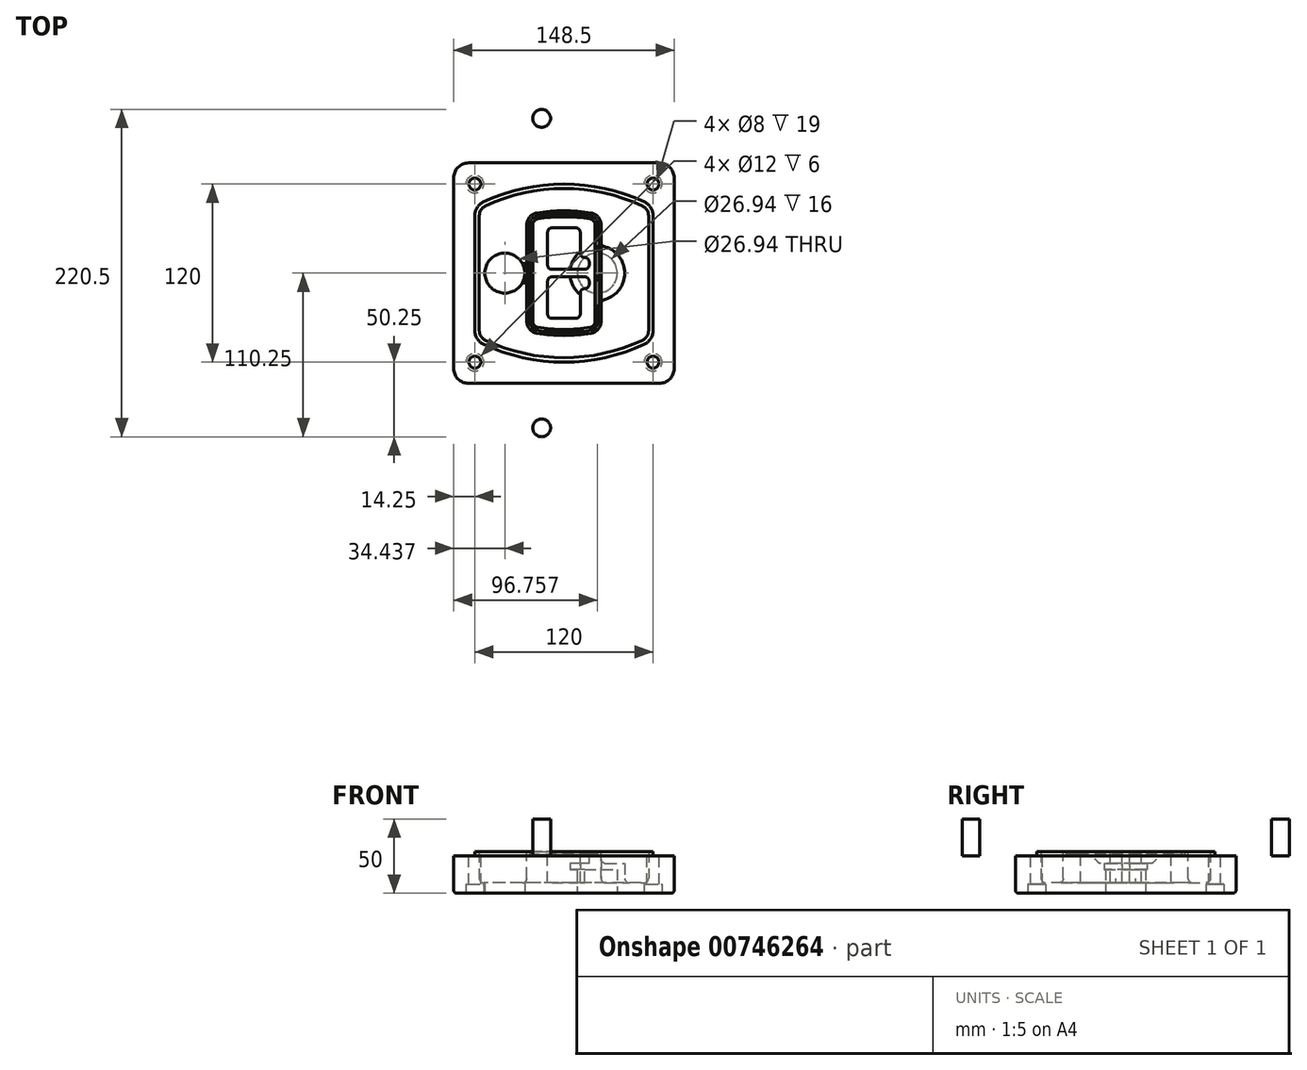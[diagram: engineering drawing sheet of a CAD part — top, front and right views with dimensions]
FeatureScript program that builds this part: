
annotation { "Feature Type Name" : "Feature", "Feature Type Description" : "" }
export const myFeature = defineFeature(function(context is Context, id is Id, definition is map)
    precondition{}
    {
        {
            var Q0;
            Q0=qCreatedBy(makeId("Top.planeOp"),FACE);
            var sketch = newSketch(context, id + "F0", { "sketchPlane" : qUnion([Q0])});
            skPoint(sketch, "E0.rect.middle", {"position": v(0, 0) * mm});
            skLineSegment(sketch, "E1.bottom", {"start": v(-64.25, -74.25) * mm, "end": v(64.25, -74.25) * mm});
            skLineSegment(sketch, "E1.top", {"start": v(-64.25, 74.25) * mm, "end": v(64.25, 74.25) * mm});
            skLineSegment(sketch, "E1.left", {"start": v(-74.25, -64.25) * mm, "end": v(-74.25, 64.25) * mm});
            skLineSegment(sketch, "E1.right", {"start": v(74.25, -64.25) * mm, "end": v(74.25, 64.25) * mm});
            skLineSegment(sketch, "E2", {"start": v(-74.25, 74.25) * mm, "end": v(74.25, -74.25) * mm, "construction": true});
            skLineSegment(sketch, "E3", {"start": v(74.25, 74.25) * mm, "end": v(-74.25, -74.25) * mm, "construction": true});
            skCircle(sketch, "E4", {"center": v(-60, 60) * mm, "radius": 4 * mm});
            skCircle(sketch, "E5", {"center": v(60, 60) * mm, "radius": 4 * mm});
            skCircle(sketch, "E6", {"center": v(60, -60) * mm, "radius": 4 * mm});
            skCircle(sketch, "E7", {"center": v(-60, -60) * mm, "radius": 4 * mm});
            skLineSegment(sketch, "E8", {"start": v(-60, 60) * mm, "end": v(60, 60) * mm, "construction": true});
            skLineSegment(sketch, "E9", {"start": v(60, 60) * mm, "end": v(60, -60) * mm, "construction": true});
            skLineSegment(sketch, "E10", {"start": v(60, -60) * mm, "end": v(-60, -60) * mm, "construction": true});
            skLineSegment(sketch, "E11", {"start": v(-60, -60) * mm, "end": v(-60, 60) * mm, "construction": true});
            skLineSegment(sketch, "E12", {"start": v(-60, 38.83) * mm, "end": v(-60, -38.83) * mm});
            skLineSegment(sketch, "E13", {"start": v(60, 38.83) * mm, "end": v(60, -38.83) * mm});
            skArc(sketch, "E14", {"start": v(54.26, 47.88) * mm, "mid": v(0, 60) * mm, "end": v(-54.26, 47.88) * mm});
            skArc(sketch, "E15", {"start": v(-54.26, -47.88) * mm, "mid": v(0, -60) * mm, "end": v(54.26, -47.88) * mm});
            skLineSegment(sketch, "E16", {"start": v(-60, 0) * mm, "end": v(60, 0) * mm, "construction": true});
            skPoint(sketch, "E17.visualSharp", {"position": v(-60, -45) * mm});
            skArc(sketch, "E17.filletArc", {"start": v(-60, -38.83) * mm, "mid": v(-58.44, -44.2) * mm, "end": v(-54.26, -47.88) * mm});
            skPoint(sketch, "E18.visualSharp", {"position": v(-60, 45) * mm});
            skArc(sketch, "E18.filletArc", {"start": v(-54.26, 47.88) * mm, "mid": v(-58.44, 44.2) * mm, "end": v(-60, 38.83) * mm});
            skPoint(sketch, "E19.visualSharp", {"position": v(60, 45) * mm});
            skArc(sketch, "E19.filletArc", {"start": v(60, 38.83) * mm, "mid": v(58.44, 44.2) * mm, "end": v(54.26, 47.88) * mm});
            skPoint(sketch, "E20.visualSharp", {"position": v(60, -45) * mm});
            skArc(sketch, "E20.filletArc", {"start": v(54.26, -47.88) * mm, "mid": v(58.44, -44.2) * mm, "end": v(60, -38.83) * mm});
            skPoint(sketch, "E21.visualSharp", {"position": v(-74.25, 74.25) * mm});
            skArc(sketch, "E21.filletArc", {"start": v(-64.25, 74.25) * mm, "mid": v(-71.32, 71.32) * mm, "end": v(-74.25, 64.25) * mm});
            skPoint(sketch, "E22.visualSharp", {"position": v(74.25, 74.25) * mm});
            skArc(sketch, "E22.filletArc", {"start": v(74.25, 64.25) * mm, "mid": v(71.32, 71.32) * mm, "end": v(64.25, 74.25) * mm});
            skPoint(sketch, "E23.visualSharp", {"position": v(74.25, -74.25) * mm});
            skArc(sketch, "E23.filletArc", {"start": v(64.25, -74.25) * mm, "mid": v(71.32, -71.32) * mm, "end": v(74.25, -64.25) * mm});
            skPoint(sketch, "E24.visualSharp", {"position": v(-74.25, -74.25) * mm});
            skArc(sketch, "E24.filletArc", {"start": v(-74.25, -64.25) * mm, "mid": v(-71.32, -71.32) * mm, "end": v(-64.25, -74.25) * mm});
            skArc(sketch, "E25.0", {"start": v(57, 38.83) * mm, "mid": v(55.9, 42.58) * mm, "end": v(52.98, 45.17) * mm});
            skLineSegment(sketch, "E25.1", {"start": v(57, 38.83) * mm, "end": v(57, -38.83) * mm});
            skArc(sketch, "E25.2", {"start": v(52.98, -45.17) * mm, "mid": v(55.9, -42.58) * mm, "end": v(57, -38.83) * mm});
            skArc(sketch, "E25.3", {"start": v(-52.98, -45.17) * mm, "mid": v(0, -57) * mm, "end": v(52.98, -45.17) * mm});
            skArc(sketch, "E25.4", {"start": v(-57, -38.83) * mm, "mid": v(-55.9, -42.58) * mm, "end": v(-52.98, -45.17) * mm});
            skArc(sketch, "E25.5", {"start": v(52.98, 45.17) * mm, "mid": v(0, 57) * mm, "end": v(-52.98, 45.17) * mm});
            skLineSegment(sketch, "E25.6", {"start": v(-57, 38.83) * mm, "end": v(-57, -38.83) * mm});
            skArc(sketch, "E25.7", {"start": v(-52.98, 45.17) * mm, "mid": v(-55.9, 42.58) * mm, "end": v(-57, 38.83) * mm});
            skArc(sketch, "E26.0", {"start": v(-55.96, 51.5) * mm, "mid": v(-61.82, 46.33) * mm, "end": v(-64, 38.83) * mm});
            skArc(sketch, "E26.1", {"start": v(55.96, 51.5) * mm, "mid": v(0, 64) * mm, "end": v(-55.96, 51.5) * mm});
            skArc(sketch, "E26.2", {"start": v(64, 38.83) * mm, "mid": v(61.82, 46.33) * mm, "end": v(55.96, 51.5) * mm});
            skLineSegment(sketch, "E26.3", {"start": v(64, 38.83) * mm, "end": v(64, -38.83) * mm});
            skArc(sketch, "E26.4", {"start": v(55.96, -51.5) * mm, "mid": v(61.82, -46.33) * mm, "end": v(64, -38.83) * mm});
            skLineSegment(sketch, "E26.5", {"start": v(-64, 38.83) * mm, "end": v(-64, -38.83) * mm});
            skArc(sketch, "E26.6", {"start": v(-55.96, -51.5) * mm, "mid": v(0, -64) * mm, "end": v(55.96, -51.5) * mm});
            skArc(sketch, "E26.7", {"start": v(-64, -38.83) * mm, "mid": v(-61.82, -46.33) * mm, "end": v(-55.96, -51.5) * mm});
            skSolve(sketch);
        }
        {
            var Q0;
            Q0=makeQuery(id+"F0.imprint","IMPRINT",FACE,{"disambiguationData":[TD([[makeQuery(id+"F0.imprint","IMPRINT",EDGE,{"derivedFrom":sQuery(id+"F0.wireOp",EDGE,"E1.bottom")}),1.0]])]});
            var Q1;
            Q1=makeQuery(id+"F0.imprint","IMPRINT",FACE,{"disambiguationData":[TD([[makeQuery(id+"F0.imprint","IMPRINT",EDGE,{"derivedFrom":sQuery(id+"F0.wireOp",EDGE,"E12")}),1.0]])]});
            var Q2;
            Q2=makeQuery(id+"F0.imprint","IMPRINT",FACE,{"disambiguationData":[TD([[makeQuery(id+"F0.imprint","IMPRINT",EDGE,{"derivedFrom":sQuery(id+"F0.wireOp",EDGE,"E25.0")}),1.0]])]});
            var Q3;
            Q3=makeQuery(id+"F0.imprint","IMPRINT",FACE,{"disambiguationData":[TD([[makeQuery(id+"F0.imprint","IMPRINT",EDGE,{"derivedFrom":sQuery(id+"F0.wireOp",EDGE,"E12")}),-1.0]])]});
            extrude(context, id + "F1", {"entities" : qUnion([Q0, Q1, Q2, Q3]), "oppositeDirection" : true, "depth" : 25 * mm});
        }
        {
            var Q0;
            Q0=makeQuery(id+"F0.imprint","IMPRINT",FACE,{"disambiguationData":[TD([[makeQuery(id+"F0.imprint","IMPRINT",EDGE,{"derivedFrom":sQuery(id+"F0.wireOp",EDGE,"E12")}),1.0]])]});
            extrude(context, id + "F2", {"entities" : qUnion([Q0]), "operationType" : NewBodyOperationType.ADD, "depth" : 3 * mm});
        }
        {
            var Q0;
            Q0=makeQuery(id+"F0.imprint","IMPRINT",FACE,{"disambiguationData":[TD([[makeQuery(id+"F0.imprint","IMPRINT",EDGE,{"derivedFrom":sQuery(id+"F0.wireOp",EDGE,"E25.0")}),1.0]])]});
            extrude(context, id + "F3", {"entities" : qUnion([Q0]), "operationType" : NewBodyOperationType.REMOVE, "oppositeDirection" : true, "depth" : 18 * mm});
        }
        {
            var Q0;
            Q0=makeQuery(id+"F2.opExtrude","CAP_FACE",FACE,{"disambiguationData":[OSD([sQuery(id+"F0.wireOp",EDGE,"E12"),sQuery(id+"F0.wireOp",EDGE,"E13"),sQuery(id+"F0.wireOp",EDGE,"E14"),sQuery(id+"F0.wireOp",EDGE,"E15"),sQuery(id+"F0.wireOp",EDGE,"E17.filletArc"),sQuery(id+"F0.wireOp",EDGE,"E18.filletArc"),sQuery(id+"F0.wireOp",EDGE,"E19.filletArc"),sQuery(id+"F0.wireOp",EDGE,"E20.filletArc"),sQuery(id+"F0.wireOp",EDGE,"E25.0"),sQuery(id+"F0.wireOp",EDGE,"E25.1"),sQuery(id+"F0.wireOp",EDGE,"E25.2"),sQuery(id+"F0.wireOp",EDGE,"E25.3"),sQuery(id+"F0.wireOp",EDGE,"E25.4"),sQuery(id+"F0.wireOp",EDGE,"E25.5"),sQuery(id+"F0.wireOp",EDGE,"E25.6"),sQuery(id+"F0.wireOp",EDGE,"E25.7")])],"isStart":false});
            var sketch = newSketch(context, id + "F4", { "sketchPlane" : qUnion([Q0])});
            skArc(sketch, "E27.0", {"start": v(-18.34, -40.45) * mm, "mid": v(0, -42) * mm, "end": v(18.34, -40.45) * mm});
            skArc(sketch, "E28.0", {"start": v(18.34, 40.45) * mm, "mid": v(0, 42) * mm, "end": v(-18.34, 40.45) * mm});
            skLineSegment(sketch, "E29", {"start": v(-25, 32.57) * mm, "end": v(-25, -32.57) * mm});
            skLineSegment(sketch, "E30", {"start": v(25, 32.57) * mm, "end": v(25, -32.57) * mm});
            skLineSegment(sketch, "E31", {"start": v(-25, 39.1) * mm, "end": v(25, 39.1) * mm, "construction": true});
            skLineSegment(sketch, "E32", {"start": v(-25, -39.1) * mm, "end": v(25, -39.1) * mm, "construction": true});
            skPoint(sketch, "E33.visualSharp", {"position": v(-25, 39.1) * mm});
            skArc(sketch, "E33.filletArc", {"start": v(-18.34, 40.45) * mm, "mid": v(-23.11, 37.73) * mm, "end": v(-25, 32.57) * mm});
            skPoint(sketch, "E34.visualSharp", {"position": v(25, 39.1) * mm});
            skArc(sketch, "E34.filletArc", {"start": v(25, 32.57) * mm, "mid": v(23.11, 37.73) * mm, "end": v(18.34, 40.45) * mm});
            skPoint(sketch, "E35.visualSharp", {"position": v(25, -39.1) * mm});
            skArc(sketch, "E35.filletArc", {"start": v(18.34, -40.45) * mm, "mid": v(23.11, -37.73) * mm, "end": v(25, -32.57) * mm});
            skPoint(sketch, "E36.visualSharp", {"position": v(-25, -39.1) * mm});
            skArc(sketch, "E36.filletArc", {"start": v(-25, -32.57) * mm, "mid": v(-23.11, -37.73) * mm, "end": v(-18.34, -40.45) * mm});
            skArc(sketch, "E37.0", {"start": v(52.98, 45.17) * mm, "mid": v(0, 57) * mm, "end": v(-52.98, 45.17) * mm});
            skArc(sketch, "E37.1", {"start": v(-52.98, 45.17) * mm, "mid": v(-55.9, 42.58) * mm, "end": v(-57, 38.83) * mm});
            skLineSegment(sketch, "E37.2", {"start": v(-57, 38.83) * mm, "end": v(-57, -38.83) * mm});
            skArc(sketch, "E37.3", {"start": v(-57, -38.83) * mm, "mid": v(-55.9, -42.58) * mm, "end": v(-52.98, -45.17) * mm});
            skArc(sketch, "E37.4", {"start": v(-52.98, -45.17) * mm, "mid": v(0, -57) * mm, "end": v(52.98, -45.17) * mm});
            skArc(sketch, "E37.5", {"start": v(52.98, -45.17) * mm, "mid": v(55.9, -42.58) * mm, "end": v(57, -38.83) * mm});
            skLineSegment(sketch, "E37.6", {"start": v(57, 38.83) * mm, "end": v(57, -38.83) * mm});
            skArc(sketch, "E37.7", {"start": v(57, 38.83) * mm, "mid": v(55.9, 42.58) * mm, "end": v(52.98, 45.17) * mm});
            skLineSegment(sketch, "E38.0", {"start": v(23, 32.57) * mm, "end": v(23, -32.57) * mm});
            skArc(sketch, "E38.1", {"start": v(18, -38.48) * mm, "mid": v(21.58, -36.44) * mm, "end": v(23, -32.57) * mm});
            skArc(sketch, "E38.2", {"start": v(-18, -38.48) * mm, "mid": v(0, -40) * mm, "end": v(18, -38.48) * mm});
            skArc(sketch, "E38.3", {"start": v(-23, -32.57) * mm, "mid": v(-21.58, -36.44) * mm, "end": v(-18, -38.48) * mm});
            skLineSegment(sketch, "E38.4", {"start": v(-23, 32.57) * mm, "end": v(-23, -32.57) * mm});
            skArc(sketch, "E38.5", {"start": v(23, 32.57) * mm, "mid": v(21.58, 36.44) * mm, "end": v(18, 38.48) * mm});
            skArc(sketch, "E38.6", {"start": v(-18, 38.48) * mm, "mid": v(-21.58, 36.44) * mm, "end": v(-23, 32.57) * mm});
            skArc(sketch, "E38.7", {"start": v(18, 38.48) * mm, "mid": v(0, 40) * mm, "end": v(-18, 38.48) * mm});
            skArc(sketch, "E39.0", {"start": v(21, 32.57) * mm, "mid": v(20.06, 35.15) * mm, "end": v(17.67, 36.5) * mm});
            skLineSegment(sketch, "E39.1", {"start": v(21, 32.57) * mm, "end": v(21, -32.57) * mm});
            skArc(sketch, "E39.2", {"start": v(17.67, -36.5) * mm, "mid": v(20.06, -35.15) * mm, "end": v(21, -32.57) * mm});
            skArc(sketch, "E39.3", {"start": v(-17.67, -36.5) * mm, "mid": v(0, -38) * mm, "end": v(17.67, -36.5) * mm});
            skArc(sketch, "E39.4", {"start": v(-21, -32.57) * mm, "mid": v(-20.06, -35.15) * mm, "end": v(-17.67, -36.5) * mm});
            skArc(sketch, "E39.5", {"start": v(17.67, 36.5) * mm, "mid": v(0, 38) * mm, "end": v(-17.67, 36.5) * mm});
            skLineSegment(sketch, "E39.6", {"start": v(-21, 32.57) * mm, "end": v(-21, -32.57) * mm});
            skArc(sketch, "E39.7", {"start": v(-17.67, 36.5) * mm, "mid": v(-20.06, 35.15) * mm, "end": v(-21, 32.57) * mm});
            skLineSegment(sketch, "E40", {"start": v(-25, 0) * mm, "end": v(25, 0) * mm, "construction": true});
            skLineSegment(sketch, "E41", {"start": v(-11, 5.5) * mm, "end": v(-11, 27.5) * mm});
            skLineSegment(sketch, "E42", {"start": v(-8, 30.5) * mm, "end": v(8, 30.5) * mm});
            skLineSegment(sketch, "E43", {"start": v(11, 27.5) * mm, "end": v(11, 13.5) * mm});
            skLineSegment(sketch, "E44", {"start": v(14, 10.5) * mm, "end": v(14, 10.5) * mm});
            skLineSegment(sketch, "E45", {"start": v(17, 7.5) * mm, "end": v(17, 5.5) * mm});
            skLineSegment(sketch, "E46", {"start": v(14, 2.5) * mm, "end": v(-8, 2.5) * mm});
            skPoint(sketch, "E47.visualSharp", {"position": v(-11, 30.5) * mm});
            skArc(sketch, "E47.filletArc", {"start": v(-8, 30.5) * mm, "mid": v(-10.12, 29.62) * mm, "end": v(-11, 27.5) * mm});
            skPoint(sketch, "E48.visualSharp", {"position": v(11, 30.5) * mm});
            skArc(sketch, "E48.filletArc", {"start": v(11, 27.5) * mm, "mid": v(10.12, 29.62) * mm, "end": v(8, 30.5) * mm});
            skPoint(sketch, "E49.visualSharp", {"position": v(11, 10.5) * mm});
            skArc(sketch, "E49.filletArc", {"start": v(11, 13.5) * mm, "mid": v(11.88, 11.38) * mm, "end": v(14, 10.5) * mm});
            skPoint(sketch, "E50.visualSharp", {"position": v(17, 10.5) * mm});
            skArc(sketch, "E50.filletArc", {"start": v(17, 7.5) * mm, "mid": v(16.12, 9.62) * mm, "end": v(14, 10.5) * mm});
            skPoint(sketch, "E51.visualSharp", {"position": v(17, 2.5) * mm});
            skArc(sketch, "E51.filletArc", {"start": v(14, 2.5) * mm, "mid": v(16.12, 3.38) * mm, "end": v(17, 5.5) * mm});
            skPoint(sketch, "E52.visualSharp", {"position": v(-11, 2.5) * mm});
            skArc(sketch, "E52.filletArc", {"start": v(-11, 5.5) * mm, "mid": v(-10.12, 3.38) * mm, "end": v(-8, 2.5) * mm});
            skLineSegment(sketch, "E53.0.MirrorCS", {"start": v(14, -2.5) * mm, "end": v(-8, -2.5) * mm});
            skArc(sketch, "E54.0.MirrorCS", {"start": v(-11, -5.5) * mm, "mid": v(-10.12, -3.38) * mm, "end": v(-8, -2.5) * mm});
            skLineSegment(sketch, "E55.0.MirrorCS", {"start": v(-11, -5.5) * mm, "end": v(-11, -27.5) * mm});
            skArc(sketch, "E56.0.MirrorCS", {"start": v(-8, -30.5) * mm, "mid": v(-10.12, -29.62) * mm, "end": v(-11, -27.5) * mm});
            skLineSegment(sketch, "E57.0.MirrorCS", {"start": v(-8, -30.5) * mm, "end": v(8, -30.5) * mm});
            skArc(sketch, "E58.0.MirrorCS", {"start": v(11, -27.5) * mm, "mid": v(10.12, -29.62) * mm, "end": v(8, -30.5) * mm});
            skLineSegment(sketch, "E59.0.MirrorCS", {"start": v(11, -27.5) * mm, "end": v(11, -13.5) * mm});
            skArc(sketch, "E60.0.MirrorCS", {"start": v(11, -13.5) * mm, "mid": v(11.88, -11.38) * mm, "end": v(14, -10.5) * mm});
            skArc(sketch, "E61.0.MirrorCS", {"start": v(17, -7.5) * mm, "mid": v(16.12, -9.62) * mm, "end": v(14, -10.5) * mm});
            skLineSegment(sketch, "E62.0.MirrorCS", {"start": v(17, -7.5) * mm, "end": v(17, -5.5) * mm});
            skArc(sketch, "E63.0.MirrorCS", {"start": v(14, -2.5) * mm, "mid": v(16.12, -3.38) * mm, "end": v(17, -5.5) * mm});
            skSolve(sketch);
        }
        {
            var Q0;
            Q0=makeQuery(id+"F4.imprint","IMPRINT",FACE,{"disambiguationData":[TD([[makeQuery(id+"F4.imprint","IMPRINT",EDGE,{"derivedFrom":sQuery(id+"F4.wireOp",EDGE,"E27.0")}),1.0]])]});
            var Q1;
            Q1=makeQuery(id+"F4.imprint","IMPRINT",FACE,{"disambiguationData":[TD([[makeQuery(id+"F4.imprint","IMPRINT",EDGE,{"derivedFrom":sQuery(id+"F4.wireOp",EDGE,"E38.0")}),-1.0]])]});
            var Q2;
            Q2=makeQuery(id+"F4.imprint","IMPRINT",FACE,{"disambiguationData":[TD([[makeQuery(id+"F4.imprint","IMPRINT",EDGE,{"derivedFrom":sQuery(id+"F4.wireOp",EDGE,"E39.0")}),1.0]])]});
            extrude(context, id + "F5", {"entities" : qUnion([Q0, Q1, Q2]), "operationType" : NewBodyOperationType.ADD, "endBound" : BoundingType.UP_TO_NEXT, "oppositeDirection" : true, "depth" : 25 * mm});
        }
        {
            var Q0;
            Q0=makeQuery(id+"F4.imprint","IMPRINT",FACE,{"disambiguationData":[TD([[makeQuery(id+"F4.imprint","IMPRINT",EDGE,{"derivedFrom":sQuery(id+"F4.wireOp",EDGE,"E38.0")}),-1.0]])]});
            extrude(context, id + "F6", {"entities" : qUnion([Q0]), "operationType" : NewBodyOperationType.REMOVE, "oppositeDirection" : true, "depth" : 2 * mm});
        }
        {
            var Q0;
            Q0=makeQuery(id+"F1.opExtrude","CAP_FACE",FACE,{"disambiguationData":[OSD([sQuery(id+"F0.wireOp",EDGE,"E1.bottom"),sQuery(id+"F0.wireOp",EDGE,"E1.top"),sQuery(id+"F0.wireOp",EDGE,"E1.left"),sQuery(id+"F0.wireOp",EDGE,"E1.right"),sQuery(id+"F0.wireOp",EDGE,"E4"),sQuery(id+"F0.wireOp",EDGE,"E5"),sQuery(id+"F0.wireOp",EDGE,"E6"),sQuery(id+"F0.wireOp",EDGE,"E7"),sQuery(id+"F0.wireOp",EDGE,"E21.filletArc"),sQuery(id+"F0.wireOp",EDGE,"E22.filletArc"),sQuery(id+"F0.wireOp",EDGE,"E23.filletArc"),sQuery(id+"F0.wireOp",EDGE,"E24.filletArc")])],"isStart":false});
            var sketch = newSketch(context, id + "F7", { "sketchPlane" : qUnion([Q0])});
            skCircle(sketch, "E64", {"center": v(22.5, 0) * mm, "radius": 13.47 * mm});
            skCircle(sketch, "E65", {"center": v(-39.81, 0) * mm, "radius": 13.47 * mm});
            skLineSegment(sketch, "E66", {"start": v(74.25, 0) * mm, "end": v(-74.25, 0) * mm});
            skCircle(sketch, "E67", {"center": v(22.5, 0) * mm, "radius": 18.47 * mm});
            skCircle(sketch, "E68", {"center": v(60, -60) * mm, "radius": 6 * mm});
            skCircle(sketch, "E69", {"center": v(-60, -60) * mm, "radius": 6 * mm});
            skCircle(sketch, "E70", {"center": v(-60, 60) * mm, "radius": 6 * mm});
            skCircle(sketch, "E71", {"center": v(60, 60) * mm, "radius": 6 * mm});
            skSolve(sketch);
        }
        {
            var Q0;
            {var subQ1=sQuery(id+"F7.wireOp",EDGE,"E66");var subQ4=sQuery(id+"F7.wireOp",EDGE,"E64");var subQ6=makeQuery(id+"F7.imprint","INTERSECT",VERTEX,{"disambiguationData":[OD(0.0)],"derivedFrom":[subQ4,subQ1]});Q0=makeQuery(id+"F7.imprint","IMPRINT",FACE,{"disambiguationData":[TD([[makeQuery(id+"F7.imprint","IMPRINT",EDGE,{"disambiguationData":[TD([[subQ6,-1.0]])],"derivedFrom":subQ4}),-1.0]])]});}
            var Q1;
            {var subQ0=sQuery(id+"F7.wireOp",EDGE,"E66");var subQ1=sQuery(id+"F7.wireOp",EDGE,"E64");var subQ3=makeQuery(id+"F7.imprint","INTERSECT",VERTEX,{"disambiguationData":[OD(0.0)],"derivedFrom":[subQ1,subQ0]});Q1=makeQuery(id+"F7.imprint","IMPRINT",FACE,{"disambiguationData":[TD([[makeQuery(id+"F7.imprint","IMPRINT",EDGE,{"disambiguationData":[TD([[subQ3,-1.0]])],"derivedFrom":subQ1}),1.0]])]});}
            var Q2;
            {var subQ0=sQuery(id+"F7.wireOp",EDGE,"E66");var subQ1=sQuery(id+"F7.wireOp",EDGE,"E64");var subQ3=makeQuery(id+"F7.imprint","INTERSECT",VERTEX,{"disambiguationData":[OD(0.0)],"derivedFrom":[subQ1,subQ0]});Q2=makeQuery(id+"F7.imprint","IMPRINT",FACE,{"disambiguationData":[TD([[makeQuery(id+"F7.imprint","IMPRINT",EDGE,{"disambiguationData":[TD([[subQ3,1.0]])],"derivedFrom":subQ1}),1.0]])]});}
            var Q3;
            {var subQ1=sQuery(id+"F7.wireOp",EDGE,"E66");var subQ4=sQuery(id+"F7.wireOp",EDGE,"E64");var subQ6=makeQuery(id+"F7.imprint","INTERSECT",VERTEX,{"disambiguationData":[OD(0.0)],"derivedFrom":[subQ4,subQ1]});Q3=makeQuery(id+"F7.imprint","IMPRINT",FACE,{"disambiguationData":[TD([[makeQuery(id+"F7.imprint","IMPRINT",EDGE,{"disambiguationData":[TD([[subQ6,1.0]])],"derivedFrom":subQ4}),-1.0]])]});}
            extrude(context, id + "F8", {"entities" : qUnion([Q0, Q1, Q2, Q3]), "operationType" : NewBodyOperationType.ADD, "oppositeDirection" : true, "depth" : 20 * mm});
        }
        {
            var Q0;
            {var subQ0=sQuery(id+"F7.wireOp",EDGE,"E66");var subQ1=sQuery(id+"F7.wireOp",EDGE,"E64");var subQ3=makeQuery(id+"F7.imprint","INTERSECT",VERTEX,{"disambiguationData":[OD(0.0)],"derivedFrom":[subQ1,subQ0]});Q0=makeQuery(id+"F7.imprint","IMPRINT",FACE,{"disambiguationData":[TD([[makeQuery(id+"F7.imprint","IMPRINT",EDGE,{"disambiguationData":[TD([[subQ3,-1.0]])],"derivedFrom":subQ1}),1.0]])]});}
            var Q1;
            {var subQ0=sQuery(id+"F7.wireOp",EDGE,"E66");var subQ1=sQuery(id+"F7.wireOp",EDGE,"E64");var subQ3=makeQuery(id+"F7.imprint","INTERSECT",VERTEX,{"disambiguationData":[OD(0.0)],"derivedFrom":[subQ1,subQ0]});Q1=makeQuery(id+"F7.imprint","IMPRINT",FACE,{"disambiguationData":[TD([[makeQuery(id+"F7.imprint","IMPRINT",EDGE,{"disambiguationData":[TD([[subQ3,1.0]])],"derivedFrom":subQ1}),1.0]])]});}
            extrude(context, id + "F9", {"entities" : qUnion([Q0, Q1]), "operationType" : NewBodyOperationType.REMOVE, "oppositeDirection" : true, "depth" : 16 * mm});
        }
        {
            var Q0;
            {var subQ0=sQuery(id+"F7.wireOp",EDGE,"E66");var subQ1=sQuery(id+"F7.wireOp",EDGE,"E65");var subQ3=makeQuery(id+"F7.imprint","INTERSECT",VERTEX,{"disambiguationData":[OD(0.0)],"derivedFrom":[subQ1,subQ0]});Q0=makeQuery(id+"F7.imprint","IMPRINT",FACE,{"disambiguationData":[TD([[makeQuery(id+"F7.imprint","IMPRINT",EDGE,{"disambiguationData":[TD([[subQ3,-1.0]])],"derivedFrom":subQ1}),1.0]])]});}
            var Q1;
            {var subQ0=sQuery(id+"F7.wireOp",EDGE,"E66");var subQ1=sQuery(id+"F7.wireOp",EDGE,"E65");var subQ3=makeQuery(id+"F7.imprint","INTERSECT",VERTEX,{"disambiguationData":[OD(0.0)],"derivedFrom":[subQ1,subQ0]});Q1=makeQuery(id+"F7.imprint","IMPRINT",FACE,{"disambiguationData":[TD([[makeQuery(id+"F7.imprint","IMPRINT",EDGE,{"disambiguationData":[TD([[subQ3,1.0]])],"derivedFrom":subQ1}),1.0]])]});}
            extrude(context, id + "F10", {"entities" : qUnion([Q0, Q1]), "operationType" : NewBodyOperationType.REMOVE, "oppositeDirection" : true, "depth" : 25 * mm});
        }
        {
            var Q0;
            Q0=makeQuery(id+"F7.imprint","IMPRINT",FACE,{"disambiguationData":[TD([[makeQuery(id+"F7.imprint","IMPRINT",EDGE,{"derivedFrom":sQuery(id+"F7.wireOp",EDGE,"E68")}),1.0]])]});
            var Q1;
            Q1=makeQuery(id+"F7.imprint","IMPRINT",FACE,{"disambiguationData":[TD([[makeQuery(id+"F7.imprint","IMPRINT",EDGE,{"derivedFrom":makeQuery(id+"F1.opExtrude","CAP_EDGE",EDGE,{"disambiguationData":[OSD([sQuery(id+"F0.wireOp",EDGE,"E5")])],"isStart":false})}),-1.0]])]});
            var Q2;
            Q2=makeQuery(id+"F7.imprint","IMPRINT",FACE,{"disambiguationData":[TD([[makeQuery(id+"F7.imprint","IMPRINT",EDGE,{"derivedFrom":sQuery(id+"F7.wireOp",EDGE,"E69")}),1.0]])]});
            var Q3;
            Q3=makeQuery(id+"F7.imprint","IMPRINT",FACE,{"disambiguationData":[TD([[makeQuery(id+"F7.imprint","IMPRINT",EDGE,{"derivedFrom":makeQuery(id+"F1.opExtrude","CAP_EDGE",EDGE,{"disambiguationData":[OSD([sQuery(id+"F0.wireOp",EDGE,"E4")])],"isStart":false})}),-1.0]])]});
            var Q4;
            Q4=makeQuery(id+"F7.imprint","IMPRINT",FACE,{"disambiguationData":[TD([[makeQuery(id+"F7.imprint","IMPRINT",EDGE,{"derivedFrom":sQuery(id+"F7.wireOp",EDGE,"E70")}),1.0]])]});
            var Q5;
            Q5=makeQuery(id+"F7.imprint","IMPRINT",FACE,{"disambiguationData":[TD([[makeQuery(id+"F7.imprint","IMPRINT",EDGE,{"derivedFrom":makeQuery(id+"F1.opExtrude","CAP_EDGE",EDGE,{"disambiguationData":[OSD([sQuery(id+"F0.wireOp",EDGE,"E7")])],"isStart":false})}),-1.0]])]});
            var Q6;
            Q6=makeQuery(id+"F7.imprint","IMPRINT",FACE,{"disambiguationData":[TD([[makeQuery(id+"F7.imprint","IMPRINT",EDGE,{"derivedFrom":sQuery(id+"F7.wireOp",EDGE,"E71")}),1.0]])]});
            var Q7;
            Q7=makeQuery(id+"F7.imprint","IMPRINT",FACE,{"disambiguationData":[TD([[makeQuery(id+"F7.imprint","IMPRINT",EDGE,{"derivedFrom":makeQuery(id+"F1.opExtrude","CAP_EDGE",EDGE,{"disambiguationData":[OSD([sQuery(id+"F0.wireOp",EDGE,"E6")])],"isStart":false})}),-1.0]])]});
            extrude(context, id + "F11", {"entities" : qUnion([Q0, Q1, Q2, Q3, Q4, Q5, Q6, Q7]), "operationType" : NewBodyOperationType.REMOVE, "oppositeDirection" : true, "depth" : 6 * mm});
        }
        {
            var Q0;
            Q0=makeQuery(id+"F9.boolean.opBoolean","COPY",FACE,{"derivedFrom":makeQuery(id+"F9.opExtrude","CAP_FACE",FACE,{"disambiguationData":[OSD([sQuery(id+"F7.wireOp",EDGE,"E64")])],"isStart":false})});
            var sketch = newSketch(context, id + "F12", { "sketchPlane" : qUnion([Q0])});
            skArc(sketch, "E72.0", {"start": v(11, 14.45) * mm, "mid": v(6.45, 9.13) * mm, "end": v(4.2, 2.5) * mm});
            skArc(sketch, "E72.1", {"start": v(4.2, -2.5) * mm, "mid": v(6.45, -9.13) * mm, "end": v(11, -14.45) * mm});
            skLineSegment(sketch, "E73", {"start": v(4.2, -2.5) * mm, "end": v(14, -2.5) * mm});
            skLineSegment(sketch, "E74.0", {"start": v(14, 2.5) * mm, "end": v(4.2, 2.5) * mm});
            skArc(sketch, "E74.1", {"start": v(14, 2.5) * mm, "mid": v(16.12, 3.38) * mm, "end": v(17, 5.5) * mm});
            skLineSegment(sketch, "E74.2", {"start": v(17, 7.5) * mm, "end": v(17, 5.5) * mm});
            skArc(sketch, "E74.3", {"start": v(17, 7.5) * mm, "mid": v(16.12, 9.62) * mm, "end": v(14, 10.5) * mm});
            skArc(sketch, "E74.4", {"start": v(11, 13.5) * mm, "mid": v(11.88, 11.38) * mm, "end": v(14, 10.5) * mm});
            skLineSegment(sketch, "E74.5", {"start": v(11, 14.45) * mm, "end": v(11, 13.5) * mm});
            skLineSegment(sketch, "E74.7", {"start": v(14, -2.5) * mm, "end": v(4.2, -2.5) * mm});
            skArc(sketch, "E74.8", {"start": v(14, -2.5) * mm, "mid": v(16.12, -3.38) * mm, "end": v(17, -5.5) * mm});
            skLineSegment(sketch, "E74.9", {"start": v(17, -7.5) * mm, "end": v(17, -5.5) * mm});
            skArc(sketch, "E74.10", {"start": v(17, -7.5) * mm, "mid": v(16.12, -9.62) * mm, "end": v(14, -10.5) * mm});
            skArc(sketch, "E74.11", {"start": v(11, -13.5) * mm, "mid": v(11.88, -11.38) * mm, "end": v(14, -10.5) * mm});
            skLineSegment(sketch, "E74.12", {"start": v(11, -14.45) * mm, "end": v(11, -13.5) * mm});
            skPoint(sketch, "E75.orphan", {"position": v(11, -27.5) * mm});
            skPoint(sketch, "E76.orphan", {"position": v(-8, -2.5) * mm});
            skPoint(sketch, "E77.orphan", {"position": v(-8, 2.5) * mm});
            skPoint(sketch, "E78.orphan", {"position": v(11, 27.5) * mm});
            skSolve(sketch);
        }
        {
            var Q0;
            {var subQ7=sQuery(id+"F12.wireOp",EDGE,"E72.0");var subQ14=sQuery(id+"F12.wireOp",EDGE,"E72.1");var subQ16=sQuery(id+"F12.wireOp",EDGE,"E74.1");var subQ18=sQuery(id+"F12.wireOp",EDGE,"E74.8");Q0=qUnion([makeQuery(id+"F12.imprint","IMPRINT",FACE,{"disambiguationData":[TD([[makeQuery(id+"F12.imprint","IMPRINT",EDGE,{"derivedFrom":subQ7}),1.0]])]}),makeQuery(id+"F12.imprint","IMPRINT",FACE,{"disambiguationData":[TD([[makeQuery(id+"F12.imprint","IMPRINT",EDGE,{"derivedFrom":subQ14}),1.0]])]}),makeQuery(id+"F12.imprint","IMPRINT",FACE,{"disambiguationData":[TD([[makeQuery(id+"F12.imprint","IMPRINT",EDGE,{"derivedFrom":subQ16}),1.0]])]}),makeQuery(id+"F12.imprint","IMPRINT",FACE,{"disambiguationData":[TD([[makeQuery(id+"F12.imprint","IMPRINT",EDGE,{"derivedFrom":subQ18}),-1.0]])]})]);}
            var Q1;
            Q1=makeQuery(id+"F5.boolean.opBoolean","SPLIT",FACE,{"disambiguationData":[TD([makeQuery(id+"F5.opExtrude","SWEPT_FACE",FACE,{"disambiguationData":[OSD([sQuery(id+"F4.wireOp",EDGE,"E41")])]})])],"derivedFrom":makeQuery(id+"F3.boolean.opBoolean","COPY",FACE,{"derivedFrom":makeQuery(id+"F3.opExtrude","CAP_FACE",FACE,{"disambiguationData":[OSD([sQuery(id+"F0.wireOp",EDGE,"E25.0"),sQuery(id+"F0.wireOp",EDGE,"E25.1"),sQuery(id+"F0.wireOp",EDGE,"E25.2"),sQuery(id+"F0.wireOp",EDGE,"E25.3"),sQuery(id+"F0.wireOp",EDGE,"E25.4"),sQuery(id+"F0.wireOp",EDGE,"E25.5"),sQuery(id+"F0.wireOp",EDGE,"E25.6"),sQuery(id+"F0.wireOp",EDGE,"E25.7")])],"isStart":false})})});
            extrude(context, id + "F13", {"entities" : qUnion([Q0]), "operationType" : NewBodyOperationType.REMOVE, "endBound" : BoundingType.UP_TO_SURFACE, "endBoundEntityFace" : qUnion([Q1]), "depth" : 25 * mm});
        }
        {
            var Q0;
            Q0=makeQuery(id+"F3.boolean.opBoolean","COPY",EDGE,{"derivedFrom":makeQuery(id+"F3.opExtrude","CAP_EDGE",EDGE,{"disambiguationData":[OSD([sQuery(id+"F0.wireOp",EDGE,"E25.6")])],"isStart":false})});
            var Q1;
            Q1=makeQuery(id+"F8.boolean.opBoolean","INTERSECT",EDGE,{"derivedFrom":[makeQuery(id+"F5.opExtrude","SWEPT_FACE",FACE,{"disambiguationData":[OSD([sQuery(id+"F4.wireOp",EDGE,"E30")])]}),makeQuery(id+"F8.opExtrude","CAP_FACE",FACE,{"disambiguationData":[OSD([sQuery(id+"F7.wireOp",EDGE,"E67")])],"isStart":false})]});
            var Q2;
            Q2=makeQuery(id+"F8.boolean.opBoolean","INTERSECT",EDGE,{"disambiguationData":[OD(1.0)],"derivedFrom":[makeQuery(id+"F5.opExtrude","SWEPT_FACE",FACE,{"disambiguationData":[OSD([sQuery(id+"F4.wireOp",EDGE,"E30")])]}),makeQuery(id+"F8.opExtrude","SWEPT_FACE",FACE,{"disambiguationData":[OSD([sQuery(id+"F7.wireOp",EDGE,"E67")])]})]});
            var Q3;
            {var subQ0=sQuery(id+"F4.wireOp",EDGE,"E30");Q3=makeQuery(id+"F8.boolean.opBoolean","SPLIT",EDGE,{"disambiguationData":[TD([makeQuery(id+"F5.opExtrude","SWEPT_FACE",FACE,{"disambiguationData":[OSD([sQuery(id+"F4.wireOp",EDGE,"E35.filletArc")])]})])],"derivedFrom":makeQuery(id+"F5.opExtrude","CAP_EDGE",EDGE,{"disambiguationData":[OSD([subQ0])],"isStart":false})});}
            var Q4;
            {var subQ0=sQuery(id+"F0.wireOp",EDGE,"E25.7");var subQ1=sQuery(id+"F0.wireOp",EDGE,"E25.1");var subQ2=sQuery(id+"F0.wireOp",EDGE,"E25.6");var subQ3=sQuery(id+"F0.wireOp",EDGE,"E25.5");var subQ4=sQuery(id+"F0.wireOp",EDGE,"E25.4");var subQ5=sQuery(id+"F0.wireOp",EDGE,"E25.0");var subQ6=sQuery(id+"F0.wireOp",EDGE,"E25.2");var subQ7=sQuery(id+"F0.wireOp",EDGE,"E25.3");Q4=makeQuery(id+"F8.boolean.opBoolean","INTERSECT",EDGE,{"derivedFrom":[makeQuery(id+"F5.boolean.opBoolean","SPLIT",FACE,{"disambiguationData":[TD([makeQuery(id+"F2.opExtrude","SWEPT_FACE",FACE,{"disambiguationData":[OSD([subQ5])]})])],"derivedFrom":makeQuery(id+"F3.boolean.opBoolean","COPY",FACE,{"derivedFrom":makeQuery(id+"F3.opExtrude","CAP_FACE",FACE,{"disambiguationData":[OSD([subQ5,subQ1,subQ6,subQ7,subQ4,subQ3,subQ2,subQ0])],"isStart":false})})}),makeQuery(id+"F8.opExtrude","SWEPT_FACE",FACE,{"disambiguationData":[OSD([sQuery(id+"F7.wireOp",EDGE,"E67")])]})]});}
            var Q5;
            Q5=makeQuery(id+"F8.boolean.opBoolean","INTERSECT",EDGE,{"disambiguationData":[OD(0.0)],"derivedFrom":[makeQuery(id+"F5.opExtrude","SWEPT_FACE",FACE,{"disambiguationData":[OSD([sQuery(id+"F4.wireOp",EDGE,"E30")])]}),makeQuery(id+"F8.opExtrude","SWEPT_FACE",FACE,{"disambiguationData":[OSD([sQuery(id+"F7.wireOp",EDGE,"E67")])]})]});
            fillet(context, id + "F14", {"entities" : qUnion([Q0, Q1, Q2, Q3, Q4, Q5]), "radius" : 3 * mm, "tangentPropagation" : true, "allowEdgeOverflow" : false});
        }
        {
            var Q0;
            Q0=makeQuery(id+"F1.opExtrude","CAP_EDGE",EDGE,{"disambiguationData":[OSD([sQuery(id+"F0.wireOp",EDGE,"E1.bottom")])],"isStart":false});
            fillet(context, id + "F15", {"entities" : qUnion([Q0]), "radius" : 2 * mm, "tangentPropagation" : true, "allowEdgeOverflow" : false});
        }
        {
            var Q0;
            {var subQ0=sQuery(id+"F0.wireOp",EDGE,"E21.filletArc");var subQ1=sQuery(id+"F0.wireOp",EDGE,"E7");var subQ2=sQuery(id+"F0.wireOp",EDGE,"E6");var subQ3=sQuery(id+"F0.wireOp",EDGE,"E5");var subQ4=sQuery(id+"F0.wireOp",EDGE,"E4");var subQ5=sQuery(id+"F0.wireOp",EDGE,"E22.filletArc");var subQ6=sQuery(id+"F0.wireOp",EDGE,"E1.bottom");var subQ7=sQuery(id+"F0.wireOp",EDGE,"E1.right");var subQ8=sQuery(id+"F0.wireOp",EDGE,"E1.top");var subQ9=sQuery(id+"F0.wireOp",EDGE,"E1.left");var subQ10=sQuery(id+"F0.wireOp",EDGE,"E23.filletArc");var subQ11=sQuery(id+"F0.wireOp",EDGE,"E24.filletArc");Q0=makeQuery(id+"F2.boolean.opBoolean","SPLIT",FACE,{"disambiguationData":[TD([makeQuery(id+"F1.opExtrude","SWEPT_FACE",FACE,{"disambiguationData":[OSD([subQ6])]})])],"derivedFrom":makeQuery(id+"F1.opExtrude","CAP_FACE",FACE,{"disambiguationData":[OSD([subQ6,subQ8,subQ9,subQ7,subQ4,subQ3,subQ2,subQ1,subQ0,subQ5,subQ10,subQ11])],"isStart":true})});}
            var sketch = newSketch(context, id + "F16", { "sketchPlane" : qUnion([Q0])});
            skLineSegment(sketch, "E79", {"start": v(-47.23, 74.25) * mm, "end": v(-30, 92.25) * mm});
            skLineSegment(sketch, "E80", {"start": v(18, 74.25) * mm, "end": v(0, 92.25) * mm});
            skLineSegment(sketch, "E81", {"start": v(-30, 92.25) * mm, "end": v(-30, 104.25) * mm});
            skLineSegment(sketch, "E82", {"start": v(0, 92.25) * mm, "end": v(0, 104.25) * mm});
            skArc(sketch, "E83", {"start": v(0, 104.25) * mm, "mid": v(-15, 119.25) * mm, "end": v(-30, 104.25) * mm});
            skLineSegment(sketch, "E84", {"start": v(-15, 104.25) * mm, "end": v(-15, 74.25) * mm, "construction": true});
            skPoint(sketch, "E84.endSnap0", {"position": v(0, 74.25) * mm});
            skCircle(sketch, "E85", {"center": v(-15, 104.25) * mm, "radius": 6 * mm});
            skLineSegment(sketch, "E86", {"start": v(-74.25, 0) * mm, "end": v(74.25, 0) * mm, "construction": true});
            skLineSegment(sketch, "E87.MirrorCS", {"start": v(-47.23, -74.25) * mm, "end": v(-30, -92.25) * mm});
            skLineSegment(sketch, "E88.MirrorCS", {"start": v(-30, -92.25) * mm, "end": v(-30, -104.25) * mm});
            skArc(sketch, "E89.MirrorCS", {"start": v(0, -104.25) * mm, "mid": v(-15, -119.25) * mm, "end": v(-30, -104.25) * mm});
            skLineSegment(sketch, "E90.MirrorCS", {"start": v(0, -92.25) * mm, "end": v(0, -104.25) * mm});
            skLineSegment(sketch, "E91.MirrorCS", {"start": v(18, -74.25) * mm, "end": v(0, -92.25) * mm});
            skCircle(sketch, "E92.MirrorC", {"center": v(-15, -104.25) * mm, "radius": 6 * mm});
            skSolve(sketch);
        }
        {
            var Q0;
            Q0 = qSketchRegion(id + "F16", true);
            extrude(context, id + "F17", {"entities" : qUnion([Q0]), "depth" : 25 * mm, "offsetDistance" : 25 * mm});
        }
        {
            var Q0;
            {var subQ0=sQuery(id+"F0.wireOp",EDGE,"E21.filletArc");var subQ1=sQuery(id+"F0.wireOp",EDGE,"E7");var subQ2=sQuery(id+"F0.wireOp",EDGE,"E6");var subQ3=sQuery(id+"F0.wireOp",EDGE,"E5");var subQ4=sQuery(id+"F0.wireOp",EDGE,"E4");var subQ5=sQuery(id+"F0.wireOp",EDGE,"E22.filletArc");var subQ6=sQuery(id+"F0.wireOp",EDGE,"E1.bottom");var subQ7=sQuery(id+"F0.wireOp",EDGE,"E1.right");var subQ8=sQuery(id+"F0.wireOp",EDGE,"E1.top");var subQ9=sQuery(id+"F0.wireOp",EDGE,"E1.left");var subQ10=sQuery(id+"F0.wireOp",EDGE,"E23.filletArc");var subQ11=sQuery(id+"F0.wireOp",EDGE,"E24.filletArc");Q0=makeQuery(id+"F2.boolean.opBoolean","SPLIT",FACE,{"disambiguationData":[TD([makeQuery(id+"F1.opExtrude","SWEPT_FACE",FACE,{"disambiguationData":[OSD([subQ6])]})])],"derivedFrom":makeQuery(id+"F1.opExtrude","CAP_FACE",FACE,{"disambiguationData":[OSD([subQ6,subQ8,subQ9,subQ7,subQ4,subQ3,subQ2,subQ1,subQ0,subQ5,subQ10,subQ11])],"isStart":true})});}
            var sketch = newSketch(context, id + "F18", { "sketchPlane" : qUnion([Q0])});
            skSolve(sketch);
        }
    });
